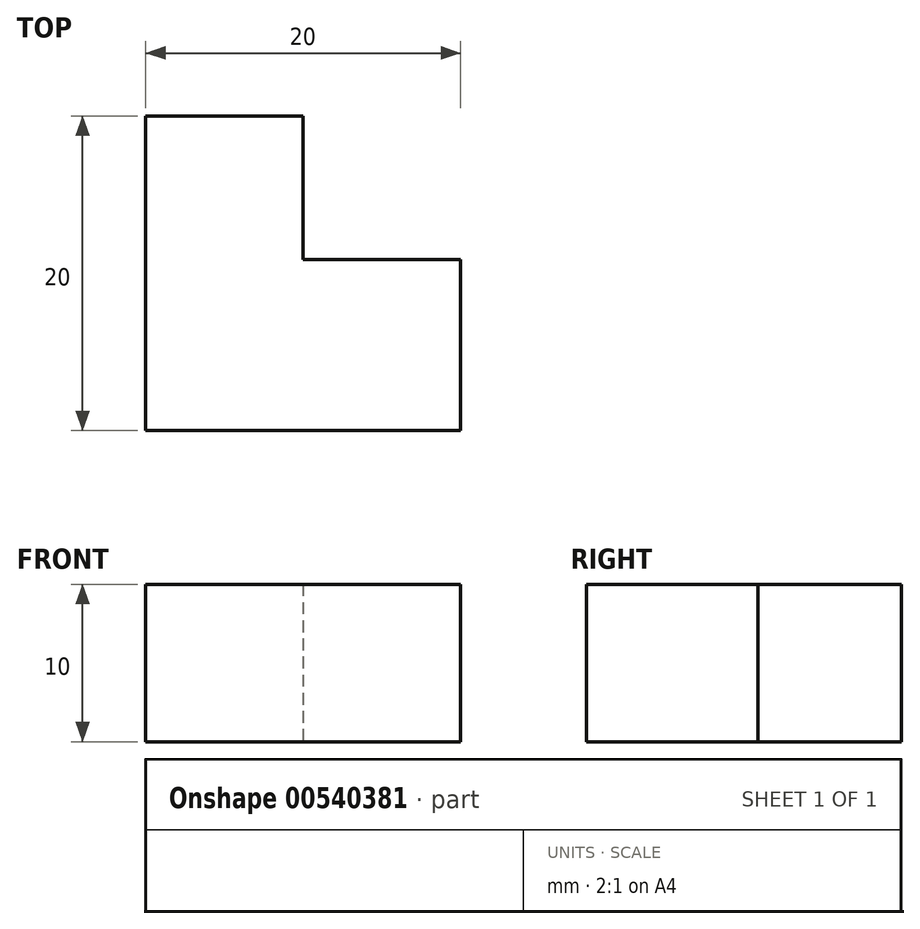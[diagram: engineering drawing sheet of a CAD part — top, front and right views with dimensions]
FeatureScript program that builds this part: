
annotation { "Feature Type Name" : "Feature", "Feature Type Description" : "" }
export const myFeature = defineFeature(function(context is Context, id is Id, definition is map)
    precondition{}
    {
        {
            var Q0;
            Q0=qCreatedBy(makeId("Top.planeOp"),FACE);
            var sketch = newSketch(context, id + "F0", { "sketchPlane" : qUnion([Q0])});
            skLineSegment(sketch, "E0", {"start": v(-10, -4.97) * mm, "end": v(10, -4.97) * mm});
            skLineSegment(sketch, "E1", {"start": v(10, -4.97) * mm, "end": v(10, 5.92) * mm});
            skLineSegment(sketch, "E2", {"start": v(10, 5.92) * mm, "end": v(0, 5.92) * mm});
            skLineSegment(sketch, "E3", {"start": v(0, 5.92) * mm, "end": v(0, 15.03) * mm});
            skLineSegment(sketch, "E4", {"start": v(0, 15.03) * mm, "end": v(-10, 15.03) * mm});
            skLineSegment(sketch, "E5", {"start": v(-10, 15.03) * mm, "end": v(-10, -4.97) * mm});
            skSolve(sketch);
        }
        {
            var Q0;
            Q0=makeQuery(id+"F0.imprint","IMPRINT",FACE,{"disambiguationData":[TD([[makeQuery(id+"F0.imprint","IMPRINT",EDGE,{"derivedFrom":sQuery(id+"F0.wireOp",EDGE,"E0")}),1.0]])]});
            extrude(context, id + "F1", {"entities" : qUnion([Q0]), "depth" : 10 * mm, "offsetDistance" : 25 * mm});
        }
    });
